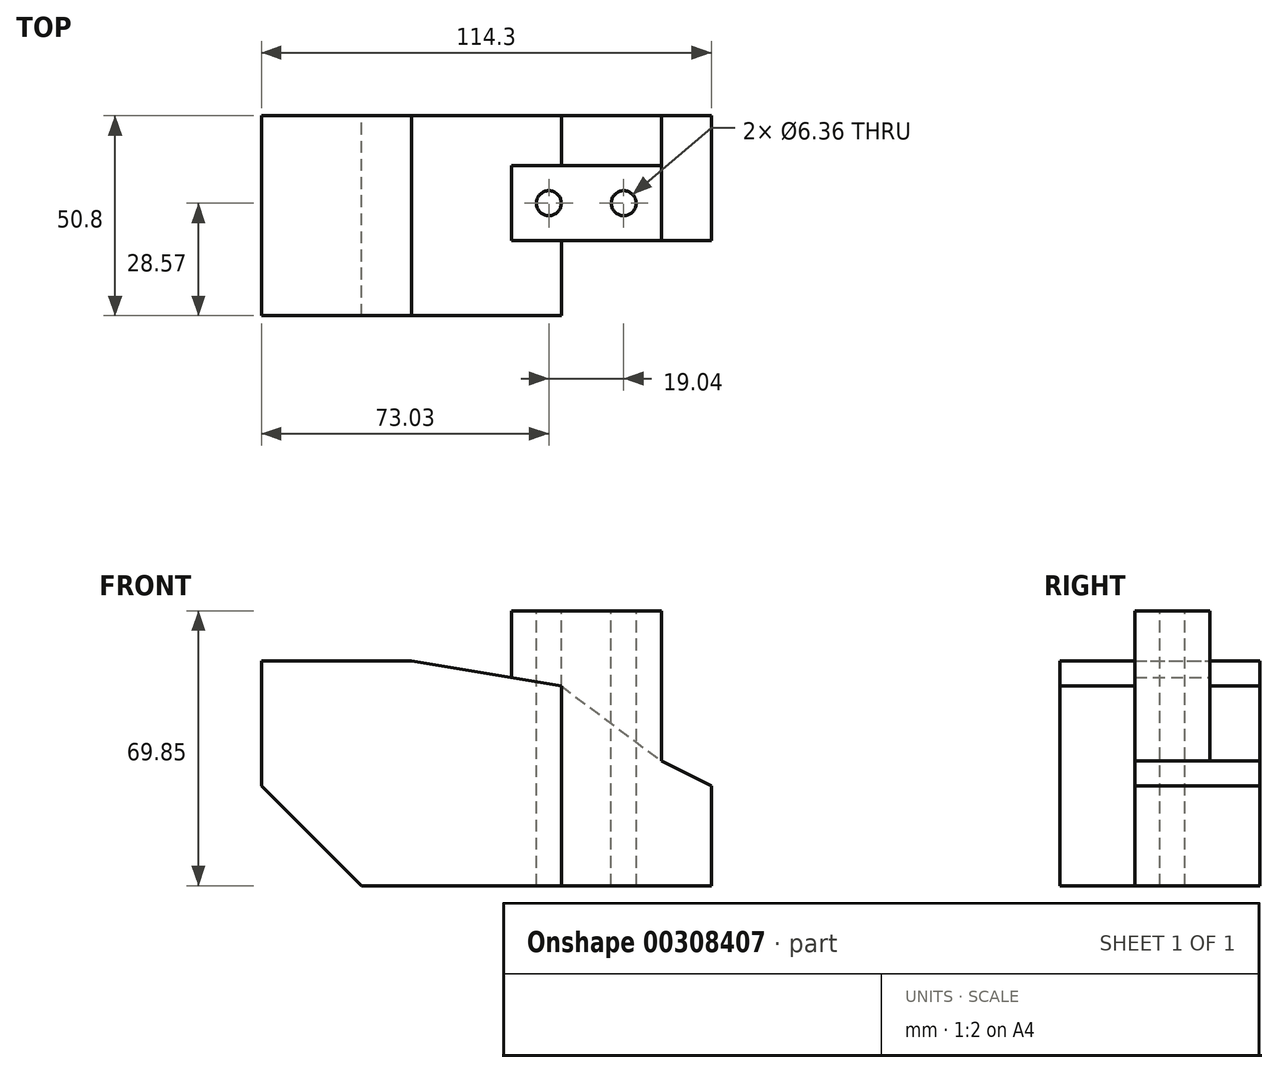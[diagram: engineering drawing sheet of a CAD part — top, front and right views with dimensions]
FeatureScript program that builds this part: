
annotation { "Feature Type Name" : "Feature", "Feature Type Description" : "" }
export const myFeature = defineFeature(function(context is Context, id is Id, definition is map)
    precondition{}
    {
        {
            var Q0;
            Q0=qCreatedBy(makeId("Front.planeOp"),FACE);
            var sketch = newSketch(context, id + "F0", { "sketchPlane" : qUnion([Q0])});
            skLineSegment(sketch, "E0", {"start": v(76.2, 0) * mm, "end": v(25.4, 0) * mm});
            skLineSegment(sketch, "E1", {"start": v(25.4, 0) * mm, "end": v(0, 25.4) * mm});
            skLineSegment(sketch, "E2", {"start": v(0, 25.4) * mm, "end": v(0, 57.15) * mm});
            skLineSegment(sketch, "E3", {"start": v(0, 57.15) * mm, "end": v(38.1, 57.15) * mm});
            skLineSegment(sketch, "E4", {"start": v(38.1, 57.15) * mm, "end": v(76.2, 50.8) * mm});
            skLineSegment(sketch, "E5", {"start": v(76.2, 50.8) * mm, "end": v(76.2, 0) * mm});
            skSolve(sketch);
        }
        {
            var Q0;
            Q0=makeQuery(id+"F0.imprint","IMPRINT",FACE,{"disambiguationData":[TD([[makeQuery(id+"F0.imprint","IMPRINT",EDGE,{"derivedFrom":sQuery(id+"F0.wireOp",EDGE,"E0")}),-1.0]])]});
            extrude(context, id + "F1", {"entities" : qUnion([Q0]), "depth" : 50.8 * mm, "symmetric" : true});
        }
        {
            var Q0;
            Q0=qCreatedBy(makeId("Front.planeOp"),FACE);
            var sketch = newSketch(context, id + "F2", { "sketchPlane" : qUnion([Q0])});
            skLineSegment(sketch, "E6.0.0", {"start": v(76.2, 0) * mm, "end": v(76.2, 50.8) * mm});
            skLineSegment(sketch, "E6.0.1", {"start": v(76.2, 50.8) * mm, "end": v(38.1, 57.15) * mm});
            skLineSegment(sketch, "E6.0.2", {"start": v(38.1, 57.15) * mm, "end": v(0, 57.15) * mm});
            skLineSegment(sketch, "E6.0.3", {"start": v(0, 57.15) * mm, "end": v(0, 25.4) * mm});
            skLineSegment(sketch, "E6.0.4", {"start": v(0, 25.4) * mm, "end": v(25.4, 0) * mm});
            skLineSegment(sketch, "E6.0.5", {"start": v(25.4, 0) * mm, "end": v(76.2, 0) * mm});
            skLineSegment(sketch, "E7", {"start": v(76.2, 50.8) * mm, "end": v(63.5, 52.92) * mm});
            skLineSegment(sketch, "E8", {"start": v(76.2, 0) * mm, "end": v(114.3, 0) * mm});
            skLineSegment(sketch, "E9", {"start": v(114.3, 0) * mm, "end": v(114.3, 25.4) * mm});
            skLineSegment(sketch, "E10", {"start": v(114.3, 25.4) * mm, "end": v(101.6, 31.75) * mm});
            skLineSegment(sketch, "E11", {"start": v(101.6, 31.75) * mm, "end": v(101.6, 69.85) * mm});
            skLineSegment(sketch, "E12", {"start": v(101.6, 69.85) * mm, "end": v(63.5, 69.85) * mm});
            skLineSegment(sketch, "E13", {"start": v(63.5, 69.85) * mm, "end": v(63.5, 52.92) * mm});
            skLineSegment(sketch, "E14", {"start": v(101.6, 31.75) * mm, "end": v(76.2, 31.75) * mm});
            skSolve(sketch);
        }
        {
            var Q0;
            {var subQ0=sQuery(id+"F2.wireOp",EDGE,"E7");Q0=makeQuery(id+"F2.imprint","IMPRINT",FACE,{"disambiguationData":[TD([[makeQuery(id+"F2.imprint","IMPRINT",EDGE,{"derivedFrom":subQ0}),-1.0]])]});}
            extrude(context, id + "F3", {"entities" : qUnion([Q0]), "depth" : 6.35 * mm, "hasSecondDirection" : true, "secondDirectionOppositeDirection" : true, "secondDirectionDepth" : 12.7 * mm});
        }
        {
            var Q0;
            {var subQ0=sQuery(id+"F2.wireOp",EDGE,"E8");Q0=makeQuery(id+"F2.imprint","IMPRINT",FACE,{"disambiguationData":[TD([[makeQuery(id+"F2.imprint","IMPRINT",EDGE,{"derivedFrom":subQ0}),1.0]])]});}
            extrude(context, id + "F4", {"entities" : qUnion([Q0]), "depth" : 6.35 * mm, "hasSecondDirection" : true, "secondDirectionOppositeDirection" : true, "secondDirectionDepth" : 25.4 * mm});
        }
        {
            var Q0;
            Q0=makeQuery(id+"F3.opExtrude","SWEPT_BODY",BODY,{"disambiguationData":[OSD([sQuery(id+"F2.wireOp",EDGE,"E6.0.0"),sQuery(id+"F2.wireOp",EDGE,"E7"),sQuery(id+"F2.wireOp",EDGE,"E11"),sQuery(id+"F2.wireOp",EDGE,"E12"),sQuery(id+"F2.wireOp",EDGE,"E13"),sQuery(id+"F2.wireOp",EDGE,"E14")])]});
            var Q1;
            Q1=makeQuery(id+"F4.opExtrude","SWEPT_BODY",BODY,{"disambiguationData":[OSD([sQuery(id+"F2.wireOp",EDGE,"E6.0.0"),sQuery(id+"F2.wireOp",EDGE,"E8"),sQuery(id+"F2.wireOp",EDGE,"E9"),sQuery(id+"F2.wireOp",EDGE,"E10"),sQuery(id+"F2.wireOp",EDGE,"E14")])]});
            var Q2;
            Q2=makeQuery(id+"F1.opExtrude","SWEPT_BODY",BODY,{"disambiguationData":[OSD([sQuery(id+"F0.wireOp",EDGE,"E0"),sQuery(id+"F0.wireOp",EDGE,"E1"),sQuery(id+"F0.wireOp",EDGE,"E2"),sQuery(id+"F0.wireOp",EDGE,"E3"),sQuery(id+"F0.wireOp",EDGE,"E4"),sQuery(id+"F0.wireOp",EDGE,"E5")])]});
            booleanBodies(context, id + "F5", {"operationType" : BooleanOperationType.UNION, "tools" : qUnion([Q0, Q1, Q2])});
        }
        {
            var Q0;
            Q0=makeQuery(id+"F5.opBoolean","MERGE",FACE,{"derivedFrom":[makeQuery(id+"F1.opExtrude","CAP_FACE",FACE,{"disambiguationData":[OSD([sQuery(id+"F0.wireOp",EDGE,"E0"),sQuery(id+"F0.wireOp",EDGE,"E1"),sQuery(id+"F0.wireOp",EDGE,"E2"),sQuery(id+"F0.wireOp",EDGE,"E3"),sQuery(id+"F0.wireOp",EDGE,"E4"),sQuery(id+"F0.wireOp",EDGE,"E5")])],"isStart":true}),makeQuery(id+"F4.opExtrude","CAP_FACE",FACE,{"disambiguationData":[OSD([sQuery(id+"F2.wireOp",EDGE,"E6.0.0"),sQuery(id+"F2.wireOp",EDGE,"E8"),sQuery(id+"F2.wireOp",EDGE,"E9"),sQuery(id+"F2.wireOp",EDGE,"E10"),sQuery(id+"F2.wireOp",EDGE,"E14")])],"isStart":true})]});
            var sketch = newSketch(context, id + "F6", { "sketchPlane" : qUnion([Q0])});
            skLineSegment(sketch, "E15", {"start": v(-76.2, 50.8) * mm, "end": v(-101.6, 31.75) * mm});
            skSolve(sketch);
        }
        {
            var Q0;
            Q0 = qSketchRegion(id + "F6", true);
            var Q1;
            Q1=makeQuery(id+"F6.imprint","IMPRINT",FACE,{"disambiguationData":[TD([[makeQuery(id+"F6.imprint","IMPRINT",EDGE,{"derivedFrom":sQuery(id+"F6.wireOp",EDGE,"E15")}),1.0]])]});
            extrude(context, id + "F7", {"entities" : qUnion([Q0, Q1]), "operationType" : NewBodyOperationType.ADD, "endBound" : BoundingType.UP_TO_NEXT, "oppositeDirection" : true, "depth" : 25.4 * mm});
        }
        {
            var Q0;
            Q0=makeQuery(id+"F3.opExtrude","SWEPT_FACE",FACE,{"disambiguationData":[OSD([sQuery(id+"F2.wireOp",EDGE,"E12")])]});
            var sketch = newSketch(context, id + "F8", { "sketchPlane" : qUnion([Q0])});
            skLineSegment(sketch, "E16", {"start": v(63.5, 3.17) * mm, "end": v(101.6, 3.17) * mm, "construction": true});
            skCircle(sketch, "E17", {"center": v(73.03, 3.17) * mm, "radius": 3.18 * mm});
            skCircle(sketch, "E18", {"center": v(92.07, 3.17) * mm, "radius": 3.18 * mm});
            skSolve(sketch);
        }
        {
            var Q0;
            Q0=makeQuery(id+"F8.imprint","IMPRINT",FACE,{"disambiguationData":[TD([[makeQuery(id+"F8.imprint","IMPRINT",EDGE,{"derivedFrom":sQuery(id+"F8.wireOp",EDGE,"E18")}),1.0]])]});
            var Q1;
            Q1=makeQuery(id+"F8.imprint","IMPRINT",FACE,{"disambiguationData":[TD([[makeQuery(id+"F8.imprint","IMPRINT",EDGE,{"derivedFrom":sQuery(id+"F8.wireOp",EDGE,"E17")}),1.0]])]});
            var Q2;
            Q2=sQuery(id+"F8.wireOp",EDGE,"E17");
            var Q3;
            Q3=sQuery(id+"F8.wireOp",EDGE,"E18");
            extrude(context, id + "F9", {"entities" : qUnion([Q0, Q1]), "operationType" : NewBodyOperationType.REMOVE, "surfaceEntities" : qUnion([Q2, Q3]), "endBound" : BoundingType.THROUGH_ALL, "oppositeDirection" : true, "depth" : 25.4 * mm});
        }
    });
